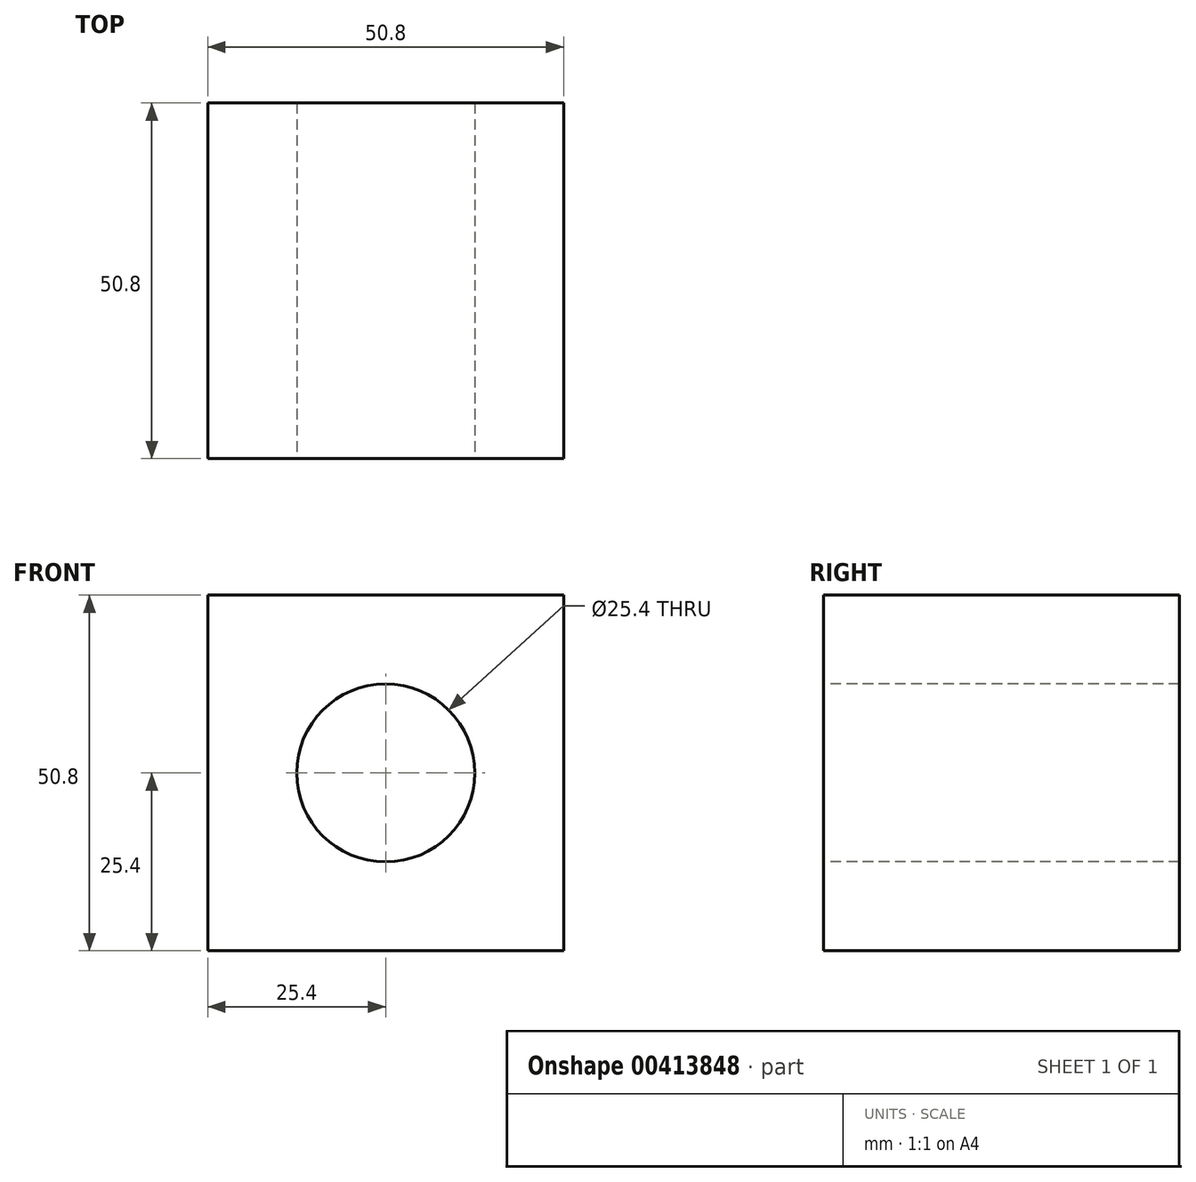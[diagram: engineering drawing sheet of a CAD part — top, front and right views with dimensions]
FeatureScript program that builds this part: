
annotation { "Feature Type Name" : "Feature", "Feature Type Description" : "" }
export const myFeature = defineFeature(function(context is Context, id is Id, definition is map)
    precondition{}
    {
        {
            var Q0;
            Q0=qCreatedBy(makeId("Top.planeOp"),FACE);
            var sketch = newSketch(context, id + "F0", { "sketchPlane" : qUnion([Q0])});
            skLineSegment(sketch, "E0.bottom", {"start": v(0, 0) * mm, "end": v(50.8, 0) * mm});
            skLineSegment(sketch, "E0.top", {"start": v(0, 50.8) * mm, "end": v(50.8, 50.8) * mm});
            skLineSegment(sketch, "E0.left", {"start": v(0, 0) * mm, "end": v(0, 50.8) * mm});
            skLineSegment(sketch, "E0.right", {"start": v(50.8, 0) * mm, "end": v(50.8, 50.8) * mm});
            skSolve(sketch);
        }
        {
            var Q0;
            Q0 = qSketchRegion(id + "F0", true);
            extrude(context, id + "F1", {"entities" : qUnion([Q0]), "depth" : 50.8 * mm, "offsetDistance" : 25.4 * mm});
        }
        {
            var Q0;
            Q0=makeQuery(id+"F1.opExtrude","SWEPT_FACE",FACE,{"disambiguationData":[OSD([sQuery(id+"F0.wireOp",EDGE,"E0.bottom")])]});
            var sketch = newSketch(context, id + "F2", { "sketchPlane" : qUnion([Q0])});
            skLineSegment(sketch, "E1", {"start": v(0, 50.8) * mm, "end": v(50.8, 0) * mm});
            skCircle(sketch, "E2", {"center": v(25.4, 25.4) * mm, "radius": 12.7 * mm});
            skSolve(sketch);
        }
        {
            var Q0;
            Q0 = qSketchRegion(id + "F2", true);
            extrude(context, id + "F3", {"entities" : qUnion([Q0]), "operationType" : NewBodyOperationType.REMOVE, "oppositeDirection" : true, "depth" : 50.8 * mm, "offsetDistance" : 25.4 * mm});
        }
    });
